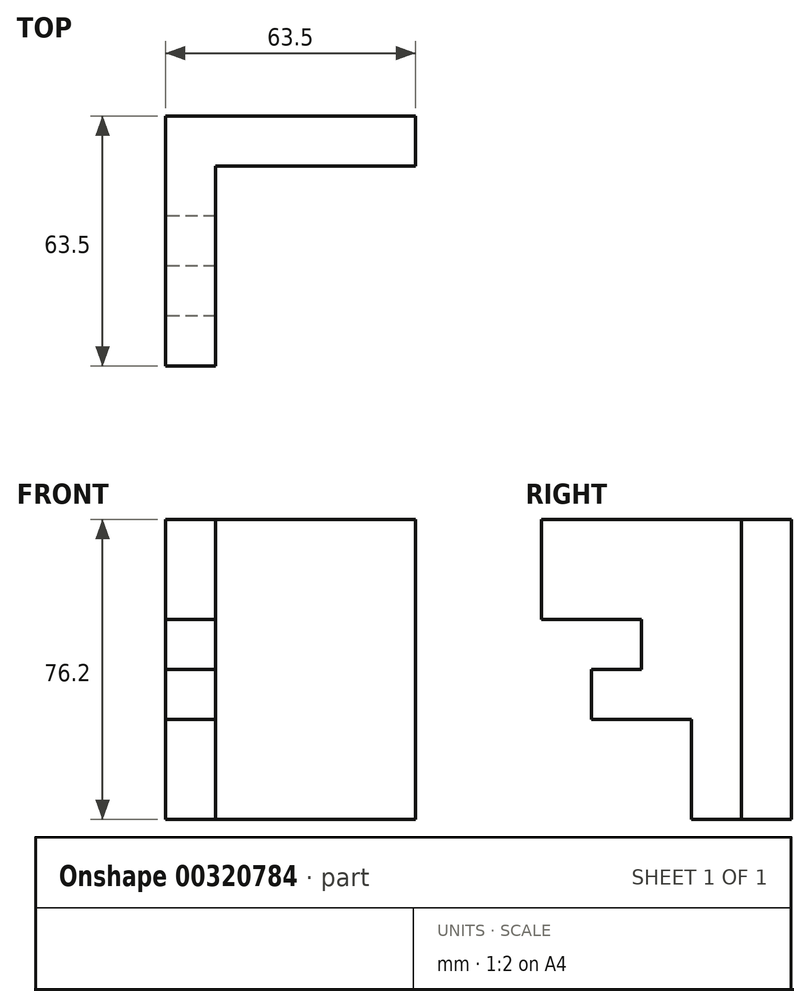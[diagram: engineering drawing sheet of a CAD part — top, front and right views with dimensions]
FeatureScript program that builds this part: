
annotation { "Feature Type Name" : "Feature", "Feature Type Description" : "" }
export const myFeature = defineFeature(function(context is Context, id is Id, definition is map)
    precondition{}
    {
        {
            var Q0;
            Q0=qCreatedBy(makeId("Right.planeOp"),FACE);
            var sketch = newSketch(context, id + "F0", { "sketchPlane" : qUnion([Q0])});
            skLineSegment(sketch, "E0", {"start": v(-22.25, 62.2) * mm, "end": v(41.25, 62.2) * mm});
            skLineSegment(sketch, "E1", {"start": v(41.25, 62.2) * mm, "end": v(41.25, -14) * mm});
            skLineSegment(sketch, "E2", {"start": v(41.25, -14) * mm, "end": v(15.85, -14) * mm});
            skLineSegment(sketch, "E3", {"start": v(15.85, -14) * mm, "end": v(15.85, 11.4) * mm});
            skLineSegment(sketch, "E4", {"start": v(15.85, 11.4) * mm, "end": v(-9.55, 11.4) * mm});
            skLineSegment(sketch, "E5", {"start": v(-9.55, 11.4) * mm, "end": v(-9.55, 24.1) * mm});
            skLineSegment(sketch, "E6", {"start": v(-22.25, 36.8) * mm, "end": v(-22.25, 62.2) * mm});
            skLineSegment(sketch, "E7", {"start": v(3.15, 36.8) * mm, "end": v(3.15, 24.1) * mm});
            skLineSegment(sketch, "E8", {"start": v(3.15, 36.8) * mm, "end": v(-22.25, 36.8) * mm});
            skLineSegment(sketch, "E9", {"start": v(-9.55, 24.1) * mm, "end": v(3.15, 24.1) * mm});
            skSolve(sketch);
        }
        {
            var Q0;
            Q0=makeQuery(id+"F0.imprint","IMPRINT",FACE,{"disambiguationData":[TD([[makeQuery(id+"F0.imprint","IMPRINT",EDGE,{"derivedFrom":sQuery(id+"F0.wireOp",EDGE,"E0")}),-1.0]])]});
            extrude(context, id + "F1", {"entities" : qUnion([Q0]), "depth" : 63.5 * mm});
        }
        {
            var Q0;
            Q0=makeQuery(id+"F1.opExtrude","CAP_FACE",FACE,{"disambiguationData":[OSD([sQuery(id+"F0.wireOp",EDGE,"E0"),sQuery(id+"F0.wireOp",EDGE,"E1"),sQuery(id+"F0.wireOp",EDGE,"E2"),sQuery(id+"F0.wireOp",EDGE,"E3"),sQuery(id+"F0.wireOp",EDGE,"E4"),sQuery(id+"F0.wireOp",EDGE,"E5"),sQuery(id+"F0.wireOp",EDGE,"E6"),sQuery(id+"F0.wireOp",EDGE,"E7"),sQuery(id+"F0.wireOp",EDGE,"E8"),sQuery(id+"F0.wireOp",EDGE,"E9")])],"isStart":false});
            var sketch = newSketch(context, id + "F2", { "sketchPlane" : qUnion([Q0])});
            skLineSegment(sketch, "E10", {"start": v(15.85, -14) * mm, "end": v(28.55, -14) * mm});
            skLineSegment(sketch, "E11", {"start": v(28.55, -14) * mm, "end": v(28.55, 62.2) * mm});
            skLineSegment(sketch, "E12", {"start": v(28.55, 62.2) * mm, "end": v(-22.25, 62.2) * mm});
            skLineSegment(sketch, "E13", {"start": v(-22.25, 62.2) * mm, "end": v(-22.25, 36.8) * mm});
            skLineSegment(sketch, "E14", {"start": v(-22.25, 36.8) * mm, "end": v(3.15, 36.8) * mm});
            skLineSegment(sketch, "E15", {"start": v(3.15, 36.8) * mm, "end": v(3.15, 24.1) * mm});
            skLineSegment(sketch, "E16", {"start": v(3.15, 24.1) * mm, "end": v(-9.55, 24.1) * mm});
            skLineSegment(sketch, "E17", {"start": v(-9.55, 24.1) * mm, "end": v(-9.55, 11.4) * mm});
            skLineSegment(sketch, "E18", {"start": v(-9.55, 11.4) * mm, "end": v(15.85, 11.4) * mm});
            skLineSegment(sketch, "E19", {"start": v(15.85, 11.4) * mm, "end": v(15.85, -14) * mm});
            skSolve(sketch);
        }
        {
            var Q0;
            Q0=makeQuery(id+"F2.imprint","IMPRINT",FACE,{"disambiguationData":[TD([[makeQuery(id+"F2.imprint","IMPRINT",EDGE,{"derivedFrom":sQuery(id+"F2.wireOp",EDGE,"E10")}),-1.0]])]});
            extrude(context, id + "F3", {"entities" : qUnion([Q0]), "operationType" : NewBodyOperationType.REMOVE, "oppositeDirection" : true, "depth" : 50.8 * mm});
        }
    });
